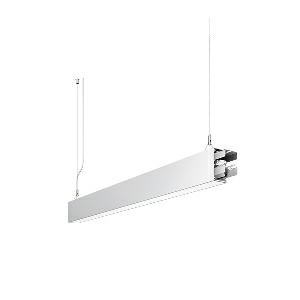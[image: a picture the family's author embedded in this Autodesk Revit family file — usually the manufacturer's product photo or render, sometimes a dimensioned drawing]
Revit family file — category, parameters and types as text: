
# Revit family: dotoo_line_-_dlp_1000_840_d_sta_00805773_8c67
name_source: partatom
category: Lighting Fixtures
units: mm (PartAtom-declared; Revit-internal decimal feet)

## family parameters
Cut with Voids When Loaded = No
Host = Face
Light Source = No
Part Type = Normal
Room Calculation Point = No
Round Connector Dimension = Use Diameter
Shared = No

## types (1)
- DOTOO.line - DLP 1000/840/D STA (1 x LED, 1000 lm, 4000K)
    Apparent Load = 10 VA
    Approval mark = CE
    CIE Flux Codes = 67 91 98 100 100
    Color Rendering = 80-89
    Color Temperature = 4000K
    Control Gear = Electronic ballast
    Default Elevation = 1800 mm
    Description = DLP 1000/840/D|Suspended luminaire|light source: LED|connected load: 220-240 V, 50/60 Hz|Power consumption: approx. 9,5 W|standby: approx. 0,20|luminous flux: 1000 lm|luminous efficacy: 105 lm/W|light distribution: Direct|direct ratio: approx. 100 %|colour temperature: Cold white, ca. 4000 K|color rendering index (CRI): >= 80|chromaticity tolerance:  3 SDCM|System of protection: IP 40|technology: Continuously dimmable|luminaire body|material: Sectional aluminium|colour: White|lamp cover: Acrylic (PMMA), Clear|mains lead: 2.00 m With free stranded wires|Fastening: Steel cable 0.3 - 0.7 m|glare control: Prism aperture|luminance(L65): <= 3000 cd/m|unified glare rating(4H 8H): <=  19|special features: DALI Load 1x, TouchDIM - dimming via standard switch, Through-wired, up to 18 m on one mains connection, Flicker-free, Suitable as emergency lighting, Start luminaire with mains connection, Mechanical and electrical connection of the individual modules without tools|
    Frequency = 50 Hz
    Height = 110 mm
    Lamp = 1 x LED
    Lamp Light Flux = 1000 lm
    Lamp count = 1
    Length = 848 mm
    Luminous efficacy = 105 lm/W
    Manufacturer = Waldmann
    ModVariant = No
    Model = 00805773
    Mounting Place = Ceiling
    Mounting Type = Pendant
    Number of Poles = 1
    OnlyDefault = Yes
    Power Factor = 1
    Product Name = DOTOO.line - DLP 1000/840/D STA
    Product group = Suspended luminaire
    ProductGroupID = 9
    Protection Class = Protection class I
    Protection Degree = IP 40
    RLX_Detail_Level = 1
    RLX_Emergency_Light_Flux = 0 lm
    RLX_Emergency_Type = 0
    RLX_Emergency_Type_DB = No
    RlxData = <blob elided: 19617 chars, md5=fbc60326>
    Socket = socket
    Standby Power = 0 W
    System Light Flux = 1000 lm
    System Power = 10 W
    Type Comments = Product without accessories
    Type Image = 113295000-00692543.jpg
    URL = http://relux.com
    VarID = ---
    Voltage = 230 V
    Voltage Range = 220-240 V
    Weight = 0.00 kg
    Width = 60 mm  [stored 0.19685 ft]

note: [stored X ft] marks values corroborated as IEEE doubles in the binary element streams (Revit-internal decimal feet)

## geometry (parser evidence)
native form markers: Blend x4, Sweep x12
no freeform markers — native parametric forms only
